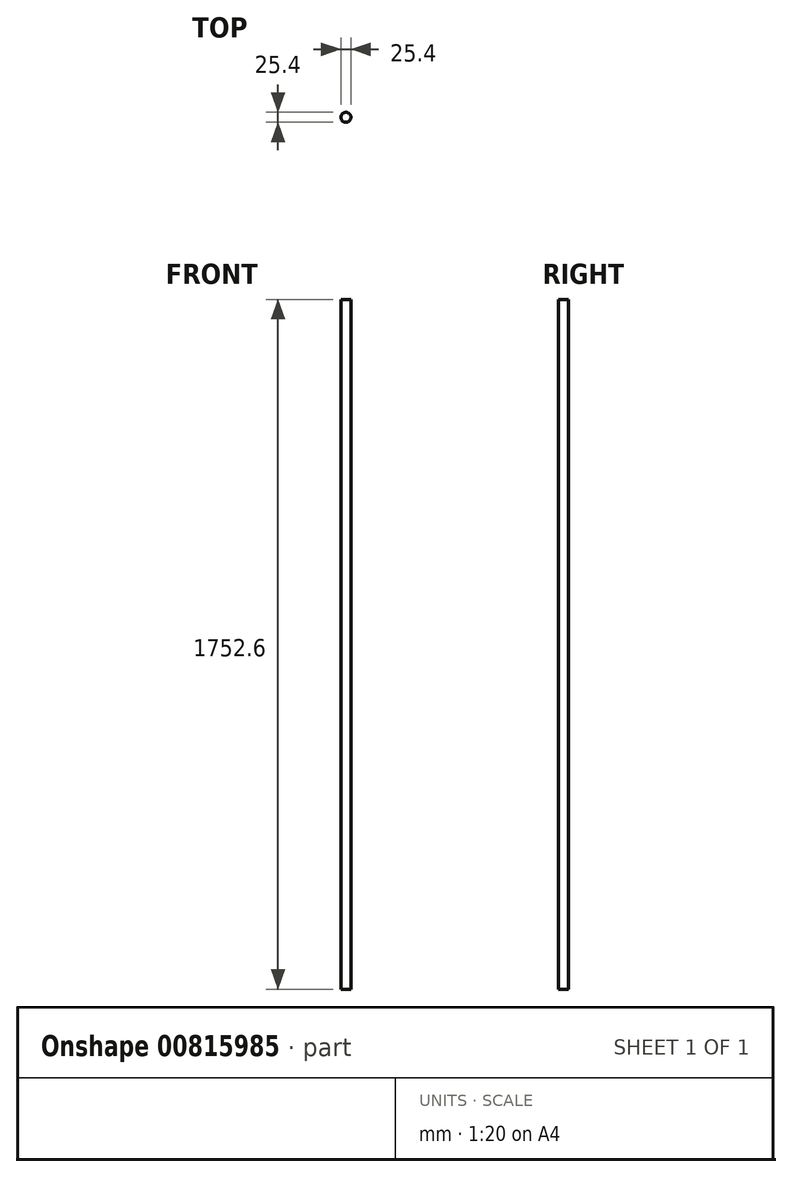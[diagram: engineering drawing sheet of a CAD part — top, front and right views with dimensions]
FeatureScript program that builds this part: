
annotation { "Feature Type Name" : "Feature", "Feature Type Description" : "" }
export const myFeature = defineFeature(function(context is Context, id is Id, definition is map)
    precondition{}
    {
        {
            var Q0;
            Q0=qCreatedBy(makeId("Top.planeOp"),FACE);
            var sketch = newSketch(context, id + "F0", { "sketchPlane" : qUnion([Q0])});
            skCircle(sketch, "E0", {"center": v(0, 0) * mm, "radius": 12.7 * mm});
            skSolve(sketch);
        }
        {
            var Q0;
            Q0 = qSketchRegion(id + "F0", true);
            extrude(context, id + "F1", {"entities" : qUnion([Q0]), "depth" : 1752.6 * mm, "offsetDistance" : 25.4 * mm});
        }
    });
